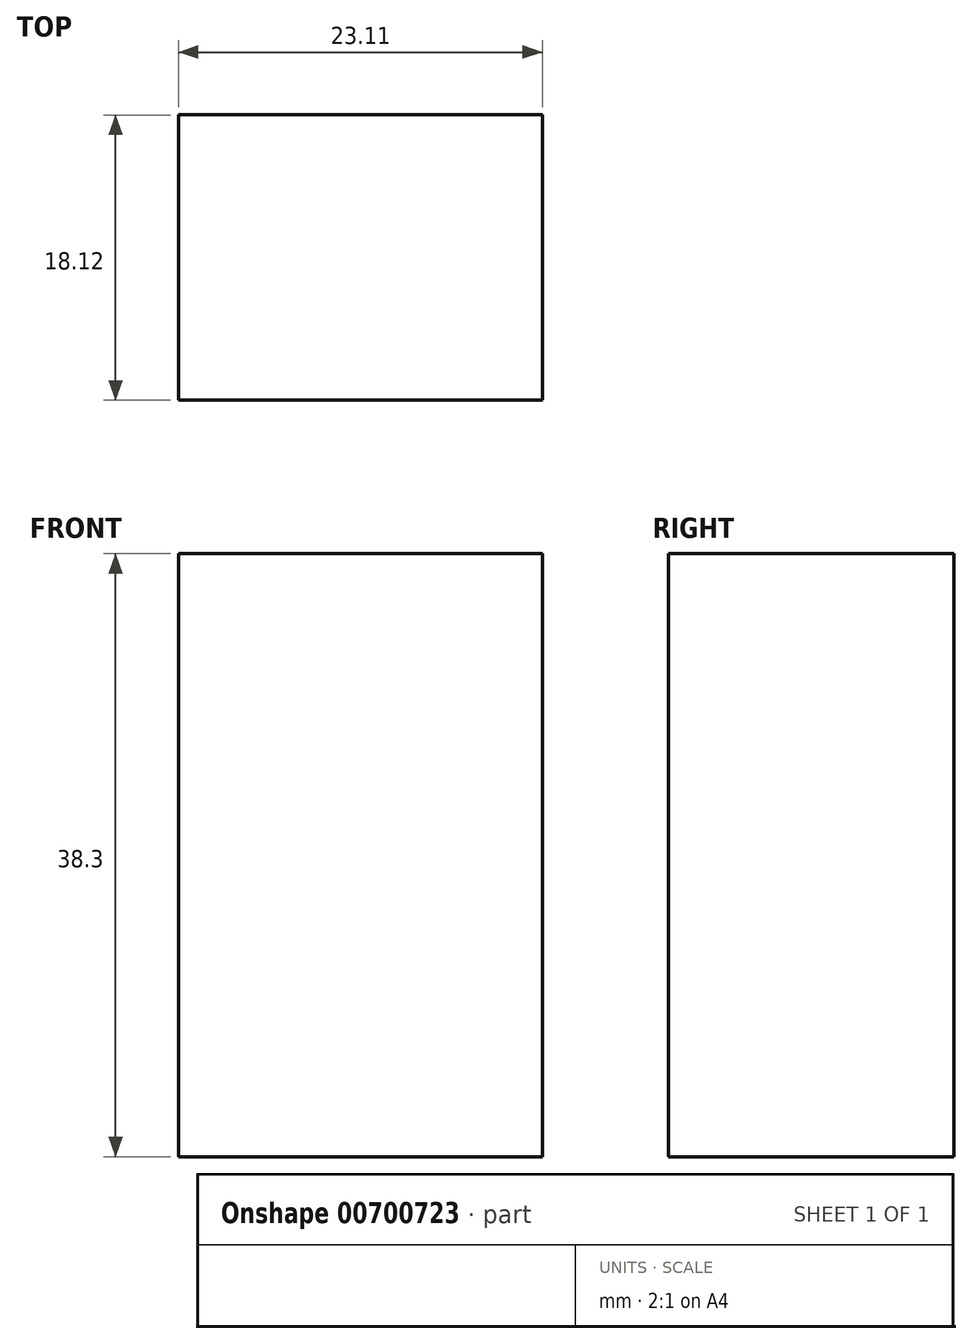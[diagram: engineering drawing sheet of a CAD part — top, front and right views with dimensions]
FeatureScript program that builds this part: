
annotation { "Feature Type Name" : "Feature", "Feature Type Description" : "" }
export const myFeature = defineFeature(function(context is Context, id is Id, definition is map)
    precondition{}
    {
        {
            var Q0;
            Q0=qCreatedBy(makeId("Top.planeOp"),FACE);
            var sketch = newSketch(context, id + "F0", { "sketchPlane" : qUnion([Q0])});
            skLineSegment(sketch, "E0.bottom", {"start": v(-30.97, 30.08) * mm, "end": v(-7.86, 30.08) * mm});
            skLineSegment(sketch, "E0.top", {"start": v(-30.97, 11.96) * mm, "end": v(-7.86, 11.96) * mm});
            skLineSegment(sketch, "E0.left", {"start": v(-30.97, 30.08) * mm, "end": v(-30.97, 11.96) * mm});
            skLineSegment(sketch, "E0.right", {"start": v(-7.86, 30.08) * mm, "end": v(-7.86, 11.96) * mm});
            skSolve(sketch);
        }
        {
            var Q0;
            Q0=makeQuery(id+"F0.imprint","IMPRINT",FACE,{"disambiguationData":[TD([[makeQuery(id+"F0.imprint","IMPRINT",EDGE,{"derivedFrom":sQuery(id+"F0.wireOp",EDGE,"E0.bottom")}),-1.0]])]});
            extrude(context, id + "F1", {"entities" : qUnion([Q0]), "depth" : 38.3 * mm, "offsetDistance" : 25.4 * mm});
        }
    });
